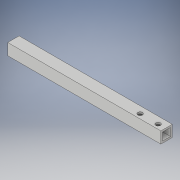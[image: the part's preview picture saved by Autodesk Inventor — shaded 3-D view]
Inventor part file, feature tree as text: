
AUTODESK INVENTOR PART (.ipt)
format: ipt  version: 2019 (Build 230136000, 136)  size: 113,152 bytes
history: native  units: mm
features: extrude x2, sketch x2
ambient origin geometry x8: Origin, YZ Plane, XZ Plane, XY Plane, X Axis, Y Axis, Z Axis, Center Point
bodies: Solid1 (feature_tree)
feature tree (4):
  extrude  "Extrusion1"  Depth=12.7mm
  extrude  "Extrusion2"  Depth=10.0mm TaperAngle=0.0deg
  sketch  "Sketch1"  dims[d0=12.7mm d1=12.7mm]
  sketch  "Sketch2"  dims[d4=170.0mm d5=0.0mm d6=10.0mm d7=0.0mm d8=5.2mm d9=8.0mm d10=5.2mm d11=20.0mm d12=5.0mm d13=2.0mm d14=2.0mm]
